# Revit family: Shroud-Lavatory-American_Standard-0062.000EC.020
name_source: partatom
category: Specialty Equipment
revit_build: Autodesk Revit 2015 (Build: 20140606_1530(x64)
units: mm (PartAtom-declared; Revit-internal decimal feet)

## types (1)
- 0062.000EC.020
    0059 Shroud Finish = Vitreous China-American Standard-020-White
    0059.020EC Shroud = No
    0062 Shroud Finish = Acrylic-American Standard-020-White
    0062.000EC Shroud = Yes
    ADA Compliant = Yes
    Assembly Code = C1030200
    Default Elevation = 0"
    Description = Shroud/Knee Contact Guard with EverClean
    Height = 10 5/32"
    Installation Type = Wall Mounted
    Length = 10 7/16"
    Manufacturer = American Standard
    Model = 0062.000EC.020
    Price = Prices may vary. Please consult Manufacturer Representative for most up-to-date price list.
    Revised Date = 01/30/2020
    URL = http://www.americanstandard-us.com
    Width = 7 27/32"

## geometry (parser evidence)
native form markers: Sweep x3
no freeform markers — native parametric forms only
